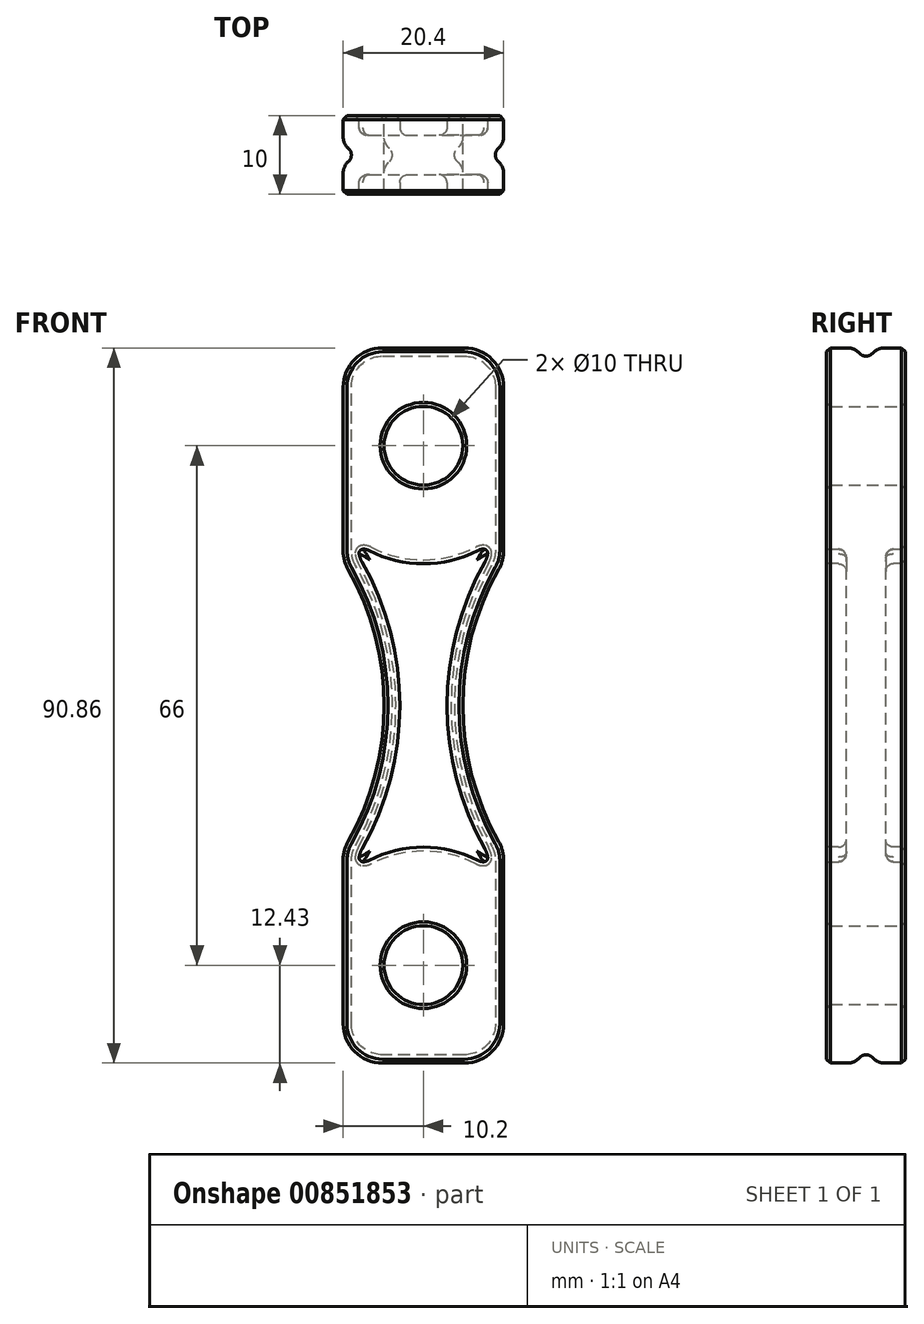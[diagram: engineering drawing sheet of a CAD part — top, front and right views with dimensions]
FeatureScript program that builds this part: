
annotation { "Feature Type Name" : "Feature", "Feature Type Description" : "" }
export const myFeature = defineFeature(function(context is Context, id is Id, definition is map)
    precondition{}
    {
        {
            var Q0;
            Q0=qCreatedBy(makeId("Front.planeOp"),FACE);
            var sketch = newSketch(context, id + "F0", { "sketchPlane" : qUnion([Q0])});
            skCircle(sketch, "E0", {"center": v(0, 33) * mm, "radius": 5 * mm});
            skCircle(sketch, "E1.MirrorC", {"center": v(0, -33) * mm, "radius": 5 * mm});
            skLineSegment(sketch, "E2.bottom", {"start": v(-5.2, 45.43) * mm, "end": v(5.2, 45.43) * mm});
            skLineSegment(sketch, "E2.top", {"start": v(-5.2, -45.43) * mm, "end": v(5.2, -45.43) * mm});
            skLineSegment(sketch, "E2.left", {"start": v(-10.2, 40.43) * mm, "end": v(-10.2, 19.73) * mm});
            skLineSegment(sketch, "E2.right", {"start": v(10.2, 40.43) * mm, "end": v(10.2, 19.73) * mm});
            skPoint(sketch, "E2.middle", {"position": v(0, 0) * mm});
            skPoint(sketch, "E3.visualSharp", {"position": v(-10.2, 45.43) * mm});
            skArc(sketch, "E3.filletArc", {"start": v(-5.2, 45.43) * mm, "mid": v(-8.74, 43.97) * mm, "end": v(-10.2, 40.43) * mm});
            skPoint(sketch, "E4.visualSharp", {"position": v(10.2, 45.43) * mm});
            skArc(sketch, "E4.filletArc", {"start": v(10.2, 40.43) * mm, "mid": v(8.74, 43.97) * mm, "end": v(5.2, 45.43) * mm});
            skPoint(sketch, "E5.visualSharp", {"position": v(-10.2, -45.43) * mm});
            skArc(sketch, "E5.filletArc", {"start": v(-10.2, -40.43) * mm, "mid": v(-8.74, -43.97) * mm, "end": v(-5.2, -45.43) * mm});
            skPoint(sketch, "E6.visualSharp", {"position": v(10.2, -45.43) * mm});
            skArc(sketch, "E6.filletArc", {"start": v(5.2, -45.43) * mm, "mid": v(8.74, -43.97) * mm, "end": v(10.2, -40.43) * mm});
            skLineSegment(sketch, "E7", {"start": v(0, 0) * mm, "end": v(-40, 0) * mm, "construction": true});
            skArc(sketch, "E8", {"start": v(-10.2, -18.36) * mm, "mid": v(-5, 0) * mm, "end": v(-10.2, 18.36) * mm});
            skLineSegment(sketch, "E9.trimOffspring", {"start": v(-10.2, -19.73) * mm, "end": v(-10.2, -40.43) * mm});
            skArc(sketch, "E10.MirrorCS", {"start": v(-10.2, 18.36) * mm, "mid": v(-5, 0) * mm, "end": v(-10.2, -18.36) * mm});
            skArc(sketch, "E11.MirrorCS", {"start": v(-9.55, -17.26) * mm, "mid": v(-5, 0) * mm, "end": v(-9.55, 17.26) * mm});
            skArc(sketch, "E12.MirrorCS", {"start": v(9.55, -17.26) * mm, "mid": v(5, 0) * mm, "end": v(9.55, 17.26) * mm});
            skLineSegment(sketch, "E13.trimOffspring", {"start": v(10.2, -19.73) * mm, "end": v(10.2, -40.43) * mm});
            skPoint(sketch, "E14.visualSharp", {"position": v(10.2, 18.36) * mm});
            skArc(sketch, "E14.filletArc", {"start": v(9.55, 17.26) * mm, "mid": v(10.04, 18.45) * mm, "end": v(10.2, 19.73) * mm});
            skPoint(sketch, "E15.visualSharp", {"position": v(-10.2, 18.36) * mm});
            skArc(sketch, "E15.filletArc", {"start": v(-10.2, 19.73) * mm, "mid": v(-10.04, 18.45) * mm, "end": v(-9.55, 17.26) * mm});
            skPoint(sketch, "E16.visualSharp", {"position": v(10.2, -18.36) * mm});
            skArc(sketch, "E16.filletArc", {"start": v(10.2, -19.73) * mm, "mid": v(10.04, -18.45) * mm, "end": v(9.55, -17.26) * mm});
            skPoint(sketch, "E17.visualSharp", {"position": v(-10.2, -18.36) * mm});
            skArc(sketch, "E17.filletArc", {"start": v(-9.55, -17.26) * mm, "mid": v(-10.04, -18.45) * mm, "end": v(-10.2, -19.73) * mm});
            skSolve(sketch);
        }
        {
            var Q0;
            Q0 = qSketchRegion(id + "F0", true);
            extrude(context, id + "F1", {"entities" : qUnion([Q0]), "depth" : 10 * mm, "offsetDistance" : 25 * mm});
        }
        {
            var Q0;
            Q0=makeQuery(id+"F1.opExtrude","CAP_EDGE",EDGE,{"disambiguationData":[OSD([sQuery(id+"F0.wireOp",EDGE,"E0")])],"isStart":false});
            var Q1;
            Q1=makeQuery(id+"F1.opExtrude","CAP_EDGE",EDGE,{"disambiguationData":[OSD([sQuery(id+"F0.wireOp",EDGE,"E0")])],"isStart":true});
            var Q2;
            Q2=makeQuery(id+"F1.opExtrude","CAP_EDGE",EDGE,{"disambiguationData":[OSD([sQuery(id+"F0.wireOp",EDGE,"E1.MirrorC")])],"isStart":false});
            var Q3;
            Q3=makeQuery(id+"F1.opExtrude","CAP_EDGE",EDGE,{"disambiguationData":[OSD([sQuery(id+"F0.wireOp",EDGE,"E1.MirrorC")])],"isStart":true});
            chamfer(context, id + "F2", {"entities" : qUnion([Q0, Q1, Q2, Q3]), "width" : 0.5 * mm, "tangentPropagation" : true});
        }
        {
            var Q0;
            Q0=qCreatedBy(makeId("Front.planeOp"),FACE);
            cPlane(context, id + "F3", {"entities" : qUnion([Q0]), "cplaneType" : CPlaneType.OFFSET, "offset" : 5 * mm, "width" : 150 * mm, "height" : 150 * mm});
        }
        {
            var Q0;
            Q0=qCreatedBy(id+"F3.planeOp",FACE);
            var sketch = newSketch(context, id + "F4", { "sketchPlane" : qUnion([Q0])});
            skArc(sketch, "E18.0.0", {"start": v(-10.2, -40.43) * mm, "mid": v(-8.74, -43.97) * mm, "end": v(-5.2, -45.43) * mm});
            skLineSegment(sketch, "E18.0.1", {"start": v(-5.2, -45.43) * mm, "end": v(5.2, -45.43) * mm});
            skArc(sketch, "E18.0.2", {"start": v(5.2, -45.43) * mm, "mid": v(8.74, -43.97) * mm, "end": v(10.2, -40.43) * mm});
            skLineSegment(sketch, "E18.0.3", {"start": v(10.2, -40.43) * mm, "end": v(10.2, -19.73) * mm});
            skArc(sketch, "E18.0.4", {"start": v(10.2, -19.73) * mm, "mid": v(10.04, -18.45) * mm, "end": v(9.55, -17.26) * mm});
            skArc(sketch, "E18.0.5", {"start": v(9.55, -17.26) * mm, "mid": v(5, 0) * mm, "end": v(9.55, 17.26) * mm});
            skArc(sketch, "E18.0.6", {"start": v(9.55, 17.26) * mm, "mid": v(10.04, 18.45) * mm, "end": v(10.2, 19.73) * mm});
            skLineSegment(sketch, "E18.0.7", {"start": v(10.2, 19.73) * mm, "end": v(10.2, 40.43) * mm});
            skArc(sketch, "E18.0.8", {"start": v(10.2, 40.43) * mm, "mid": v(8.74, 43.97) * mm, "end": v(5.2, 45.43) * mm});
            skLineSegment(sketch, "E18.0.9", {"start": v(5.2, 45.43) * mm, "end": v(-5.2, 45.43) * mm});
            skArc(sketch, "E18.0.10", {"start": v(-5.2, 45.43) * mm, "mid": v(-8.74, 43.97) * mm, "end": v(-10.2, 40.43) * mm});
            skLineSegment(sketch, "E18.0.11", {"start": v(-10.2, 40.43) * mm, "end": v(-10.2, 19.73) * mm});
            skArc(sketch, "E18.0.12", {"start": v(-10.2, 19.73) * mm, "mid": v(-10.04, 18.45) * mm, "end": v(-9.55, 17.26) * mm});
            skArc(sketch, "E18.0.13", {"start": v(-9.55, 17.26) * mm, "mid": v(-5, 0) * mm, "end": v(-9.55, -17.26) * mm});
            skArc(sketch, "E18.0.14", {"start": v(-9.55, -17.26) * mm, "mid": v(-10.04, -18.45) * mm, "end": v(-10.2, -19.73) * mm});
            skLineSegment(sketch, "E18.0.15", {"start": v(-10.2, -19.73) * mm, "end": v(-10.2, -40.43) * mm});
            skSolve(sketch);
        }
        {
            var Q0;
            Q0=qCreatedBy(makeId("Right.planeOp"),FACE);
            var sketch = newSketch(context, id + "F5", { "sketchPlane" : qUnion([Q0])});
            skCircle(sketch, "E19", {"center": v(-5, 45.5) * mm, "radius": 1.13 * mm});
            skSolve(sketch);
        }
        {
            var Q0;
            Q0=makeQuery(id+"F5.imprint","IMPRINT",FACE,{"disambiguationData":[TD([[makeQuery(id+"F5.imprint","IMPRINT",EDGE,{"derivedFrom":sQuery(id+"F5.wireOp",EDGE,"E19")}),1.0]])]});
            var Q1;
            Q1 = qConstructionFilter(qBodyType(qCreatedBy(id + "F4" ,EDGE), BodyType.WIRE), ConstructionObject.NO);
            sweep(context, id + "F6", {"operationType" : NewBodyOperationType.REMOVE, "profiles" : qUnion([Q0]), "path" : qUnion([Q1])});
        }
        {
            var Q0;
            Q0=makeQuery(id+"F6.boolean.opBoolean","INTERSECT",EDGE,{"disambiguationData":[OD(1.0)],"derivedFrom":[makeQuery(id+"F1.opExtrude","SWEPT_FACE",FACE,{"disambiguationData":[OSD([sQuery(id+"F0.wireOp",EDGE,"E4.filletArc")])]}),makeQuery(id+"F6.opSweep","SWEPT_FACE",FACE,{"disambiguationData":[OSD([sQuery(id+"F4.wireOp",EDGE,"E18.0.8"),sQuery(id+"F5.wireOp",EDGE,"E19")])]})]});
            var Q1;
            Q1=makeQuery(id+"F6.boolean.opBoolean","INTERSECT",EDGE,{"disambiguationData":[OD(0.0)],"derivedFrom":[makeQuery(id+"F1.opExtrude","SWEPT_FACE",FACE,{"disambiguationData":[OSD([sQuery(id+"F0.wireOp",EDGE,"E4.filletArc")])]}),makeQuery(id+"F6.opSweep","SWEPT_FACE",FACE,{"disambiguationData":[OSD([sQuery(id+"F4.wireOp",EDGE,"E18.0.8"),sQuery(id+"F5.wireOp",EDGE,"E19")])]})]});
            fillet(context, id + "F7", {"entities" : qUnion([Q0, Q1]), "tangentPropagation" : true, "radius" : 2 * mm, "defaultsChanged" : true, "vertexSettings" : [], "allowEdgeOverflow" : false});
        }
        {
            var Q0;
            Q0=makeQuery(id+"F1.opExtrude","CAP_FACE",FACE,{"disambiguationData":[OSD([sQuery(id+"F0.wireOp",EDGE,"E0"),sQuery(id+"F0.wireOp",EDGE,"E2.bottom"),sQuery(id+"F0.wireOp",EDGE,"E2.top"),sQuery(id+"F0.wireOp",EDGE,"E2.left"),sQuery(id+"F0.wireOp",EDGE,"E2.right"),sQuery(id+"F0.wireOp",EDGE,"E3.filletArc"),sQuery(id+"F0.wireOp",EDGE,"E4.filletArc"),sQuery(id+"F0.wireOp",EDGE,"E5.filletArc"),sQuery(id+"F0.wireOp",EDGE,"E6.filletArc"),sQuery(id+"F0.wireOp",EDGE,"E9.trimOffspring"),sQuery(id+"F0.wireOp",EDGE,"E1.MirrorC"),sQuery(id+"F0.wireOp",EDGE,"E10.MirrorCS"),sQuery(id+"F0.wireOp",EDGE,"E12.MirrorCS"),sQuery(id+"F0.wireOp",EDGE,"E13.trimOffspring"),sQuery(id+"F0.wireOp",EDGE,"E14.filletArc"),sQuery(id+"F0.wireOp",EDGE,"E15.filletArc"),sQuery(id+"F0.wireOp",EDGE,"E16.filletArc"),sQuery(id+"F0.wireOp",EDGE,"E17.filletArc")])],"isStart":false});
            var sketch = newSketch(context, id + "F8", { "sketchPlane" : qUnion([Q0])});
            skArc(sketch, "E20", {"start": v(-8.2, 20.44) * mm, "mid": v(0, 18) * mm, "end": v(8.2, 20.44) * mm});
            skArc(sketch, "E21", {"start": v(8.2, -20.44) * mm, "mid": v(0, -18) * mm, "end": v(-8.2, -20.44) * mm});
            skArc(sketch, "E22.0", {"start": v(-7.81, 18.25) * mm, "mid": v(-3, 0) * mm, "end": v(-7.81, -18.25) * mm});
            skArc(sketch, "E23.0", {"start": v(7.81, -18.25) * mm, "mid": v(3, 0) * mm, "end": v(7.81, 18.25) * mm});
            skArc(sketch, "E24.0", {"start": v(7.81, 18.25) * mm, "mid": v(8.1, 18.96) * mm, "end": v(8.2, 19.73) * mm});
            skLineSegment(sketch, "E24.1", {"start": v(8.2, 20.44) * mm, "end": v(8.2, 19.73) * mm});
            skArc(sketch, "E25.0", {"start": v(8.2, -19.73) * mm, "mid": v(8.1, -18.96) * mm, "end": v(7.81, -18.25) * mm});
            skLineSegment(sketch, "E25.1", {"start": v(8.2, -19.73) * mm, "end": v(8.2, -20.44) * mm});
            skArc(sketch, "E26.0", {"start": v(-8.2, 19.73) * mm, "mid": v(-8.1, 18.96) * mm, "end": v(-7.81, 18.25) * mm});
            skLineSegment(sketch, "E26.1", {"start": v(-8.2, 20.44) * mm, "end": v(-8.2, 19.73) * mm});
            skLineSegment(sketch, "E27.0", {"start": v(-8.2, -19.73) * mm, "end": v(-8.2, -20.44) * mm});
            skArc(sketch, "E27.1", {"start": v(-7.81, -18.25) * mm, "mid": v(-8.1, -18.96) * mm, "end": v(-8.2, -19.73) * mm});
            skSolve(sketch);
        }
        {
            var Q0;
            Q0=makeQuery(id+"F8.imprint","IMPRINT",FACE,{"disambiguationData":[TD([[makeQuery(id+"F8.imprint","IMPRINT",EDGE,{"derivedFrom":sQuery(id+"F8.wireOp",EDGE,"E20")}),-1.0]])]});
            extrude(context, id + "F9", {"entities" : qUnion([Q0]), "operationType" : NewBodyOperationType.REMOVE, "oppositeDirection" : true, "depth" : 2.5 * mm, "offsetDistance" : 25 * mm});
        }
        {
            var Q0;
            Q0=makeQuery(id+"F8.imprint","IMPRINT",FACE,{"disambiguationData":[TD([[makeQuery(id+"F8.imprint","IMPRINT",EDGE,{"derivedFrom":sQuery(id+"F8.wireOp",EDGE,"E20")}),-1.0]])]});
            extrude(context, id + "F10", {"entities" : qUnion([Q0]), "operationType" : NewBodyOperationType.REMOVE, "oppositeDirection" : true, "depth" : 34.2 * mm, "offsetDistance" : 25 * mm, "hasSecondDirection" : true, "secondDirectionOppositeDirection" : true, "secondDirectionDepth" : 7.5 * mm});
        }
        {
            var Q0;
            Q0=makeQuery(id+"F10.boolean.opBoolean","COPY",EDGE,{"derivedFrom":makeQuery(id+"F10.opExtrude","SWEPT_EDGE",EDGE,{"disambiguationData":[OSD([sQuery(id+"F8.wireOp",EDGE,"E20"),sQuery(id+"F8.wireOp",EDGE,"E24.1")])]})});
            var Q1;
            Q1=makeQuery(id+"F10.boolean.opBoolean","COPY",EDGE,{"derivedFrom":makeQuery(id+"F10.opExtrude","SWEPT_EDGE",EDGE,{"disambiguationData":[OSD([sQuery(id+"F8.wireOp",EDGE,"E20"),sQuery(id+"F8.wireOp",EDGE,"E26.1")])]})});
            var Q2;
            Q2=makeQuery(id+"F10.boolean.opBoolean","COPY",EDGE,{"derivedFrom":makeQuery(id+"F10.opExtrude","SWEPT_EDGE",EDGE,{"disambiguationData":[OSD([sQuery(id+"F8.wireOp",EDGE,"E21"),sQuery(id+"F8.wireOp",EDGE,"E25.1")])]})});
            var Q3;
            Q3=makeQuery(id+"F10.boolean.opBoolean","COPY",EDGE,{"derivedFrom":makeQuery(id+"F10.opExtrude","SWEPT_EDGE",EDGE,{"disambiguationData":[OSD([sQuery(id+"F8.wireOp",EDGE,"E21"),sQuery(id+"F8.wireOp",EDGE,"E27.0")])]})});
            var Q4;
            Q4=makeQuery(id+"F9.boolean.opBoolean","COPY",EDGE,{"derivedFrom":makeQuery(id+"F9.opExtrude","SWEPT_EDGE",EDGE,{"disambiguationData":[OSD([sQuery(id+"F8.wireOp",EDGE,"E20"),sQuery(id+"F8.wireOp",EDGE,"E26.1")])]})});
            var Q5;
            Q5=makeQuery(id+"F9.boolean.opBoolean","COPY",EDGE,{"derivedFrom":makeQuery(id+"F9.opExtrude","SWEPT_EDGE",EDGE,{"disambiguationData":[OSD([sQuery(id+"F8.wireOp",EDGE,"E20"),sQuery(id+"F8.wireOp",EDGE,"E24.1")])]})});
            var Q6;
            Q6=makeQuery(id+"F9.boolean.opBoolean","COPY",EDGE,{"derivedFrom":makeQuery(id+"F9.opExtrude","SWEPT_EDGE",EDGE,{"disambiguationData":[OSD([sQuery(id+"F8.wireOp",EDGE,"E21"),sQuery(id+"F8.wireOp",EDGE,"E25.1")])]})});
            var Q7;
            Q7=makeQuery(id+"F9.boolean.opBoolean","COPY",EDGE,{"derivedFrom":makeQuery(id+"F9.opExtrude","SWEPT_EDGE",EDGE,{"disambiguationData":[OSD([sQuery(id+"F8.wireOp",EDGE,"E21"),sQuery(id+"F8.wireOp",EDGE,"E27.0")])]})});
            fillet(context, id + "F11", {"entities" : qUnion([Q0, Q1, Q2, Q3, Q4, Q5, Q6, Q7]), "tangentPropagation" : true, "radius" : 1.5 * mm, "defaultsChanged" : false, "vertexSettings" : [], "allowEdgeOverflow" : false});
        }
        {
            var Q0;
            Q0=makeQuery(id+"F11.opFillet","BLEND_EDGE",EDGE,{"blendedFrom":[makeQuery(id+"F10.boolean.opBoolean","COPY",EDGE,{"derivedFrom":makeQuery(id+"F10.opExtrude","SWEPT_EDGE",EDGE,{"disambiguationData":[OSD([sQuery(id+"F8.wireOp",EDGE,"E20"),sQuery(id+"F8.wireOp",EDGE,"E24.1")])]})}),makeQuery(id+"F10.boolean.opBoolean","COPY",FACE,{"derivedFrom":makeQuery(id+"F10.opExtrude","SWEPT_FACE",FACE,{"disambiguationData":[OSD([sQuery(id+"F8.wireOp",EDGE,"E24.0")])]})})],"blendedInto":[makeQuery(id+"F10.boolean.opBoolean","COPY",FACE,{"derivedFrom":makeQuery(id+"F10.opExtrude","SWEPT_FACE",FACE,{"disambiguationData":[OSD([sQuery(id+"F8.wireOp",EDGE,"E24.0")])]})})]});
            var Q1;
            Q1=makeQuery(id+"F11.opFillet","BLEND_EDGE",EDGE,{"blendedFrom":[makeQuery(id+"F10.boolean.opBoolean","COPY",EDGE,{"derivedFrom":makeQuery(id+"F10.opExtrude","SWEPT_EDGE",EDGE,{"disambiguationData":[OSD([sQuery(id+"F8.wireOp",EDGE,"E20"),sQuery(id+"F8.wireOp",EDGE,"E26.1")])]})}),makeQuery(id+"F10.boolean.opBoolean","COPY",FACE,{"derivedFrom":makeQuery(id+"F10.opExtrude","SWEPT_FACE",FACE,{"disambiguationData":[OSD([sQuery(id+"F8.wireOp",EDGE,"E26.0")])]})})],"blendedInto":[makeQuery(id+"F10.boolean.opBoolean","COPY",FACE,{"derivedFrom":makeQuery(id+"F10.opExtrude","SWEPT_FACE",FACE,{"disambiguationData":[OSD([sQuery(id+"F8.wireOp",EDGE,"E26.0")])]})})]});
            var Q2;
            Q2=makeQuery(id+"F11.opFillet","BLEND_EDGE",EDGE,{"blendedFrom":[makeQuery(id+"F10.boolean.opBoolean","COPY",EDGE,{"derivedFrom":makeQuery(id+"F10.opExtrude","SWEPT_EDGE",EDGE,{"disambiguationData":[OSD([sQuery(id+"F8.wireOp",EDGE,"E21"),sQuery(id+"F8.wireOp",EDGE,"E25.1")])]})}),makeQuery(id+"F10.boolean.opBoolean","COPY",FACE,{"derivedFrom":makeQuery(id+"F10.opExtrude","SWEPT_FACE",FACE,{"disambiguationData":[OSD([sQuery(id+"F8.wireOp",EDGE,"E25.0")])]})})],"blendedInto":[makeQuery(id+"F10.boolean.opBoolean","COPY",FACE,{"derivedFrom":makeQuery(id+"F10.opExtrude","SWEPT_FACE",FACE,{"disambiguationData":[OSD([sQuery(id+"F8.wireOp",EDGE,"E25.0")])]})})]});
            var Q3;
            Q3=makeQuery(id+"F11.opFillet","BLEND_EDGE",EDGE,{"blendedFrom":[makeQuery(id+"F10.boolean.opBoolean","COPY",EDGE,{"derivedFrom":makeQuery(id+"F10.opExtrude","SWEPT_EDGE",EDGE,{"disambiguationData":[OSD([sQuery(id+"F8.wireOp",EDGE,"E21"),sQuery(id+"F8.wireOp",EDGE,"E27.0")])]})}),makeQuery(id+"F10.boolean.opBoolean","COPY",FACE,{"derivedFrom":makeQuery(id+"F10.opExtrude","SWEPT_FACE",FACE,{"disambiguationData":[OSD([sQuery(id+"F8.wireOp",EDGE,"E27.1")])]})})],"blendedInto":[makeQuery(id+"F10.boolean.opBoolean","COPY",FACE,{"derivedFrom":makeQuery(id+"F10.opExtrude","SWEPT_FACE",FACE,{"disambiguationData":[OSD([sQuery(id+"F8.wireOp",EDGE,"E27.1")])]})})]});
            var Q4;
            Q4=makeQuery(id+"F11.opFillet","BLEND_EDGE",EDGE,{"blendedFrom":[makeQuery(id+"F9.boolean.opBoolean","COPY",EDGE,{"derivedFrom":makeQuery(id+"F9.opExtrude","SWEPT_EDGE",EDGE,{"disambiguationData":[OSD([sQuery(id+"F8.wireOp",EDGE,"E21"),sQuery(id+"F8.wireOp",EDGE,"E27.0")])]})}),makeQuery(id+"F9.boolean.opBoolean","COPY",FACE,{"derivedFrom":makeQuery(id+"F9.opExtrude","SWEPT_FACE",FACE,{"disambiguationData":[OSD([sQuery(id+"F8.wireOp",EDGE,"E27.1")])]})})],"blendedInto":[makeQuery(id+"F9.boolean.opBoolean","COPY",FACE,{"derivedFrom":makeQuery(id+"F9.opExtrude","SWEPT_FACE",FACE,{"disambiguationData":[OSD([sQuery(id+"F8.wireOp",EDGE,"E27.1")])]})})]});
            var Q5;
            Q5=makeQuery(id+"F11.opFillet","BLEND_EDGE",EDGE,{"blendedFrom":[makeQuery(id+"F9.boolean.opBoolean","COPY",EDGE,{"derivedFrom":makeQuery(id+"F9.opExtrude","SWEPT_EDGE",EDGE,{"disambiguationData":[OSD([sQuery(id+"F8.wireOp",EDGE,"E21"),sQuery(id+"F8.wireOp",EDGE,"E25.1")])]})}),makeQuery(id+"F9.boolean.opBoolean","COPY",FACE,{"derivedFrom":makeQuery(id+"F9.opExtrude","SWEPT_FACE",FACE,{"disambiguationData":[OSD([sQuery(id+"F8.wireOp",EDGE,"E25.0")])]})})],"blendedInto":[makeQuery(id+"F9.boolean.opBoolean","COPY",FACE,{"derivedFrom":makeQuery(id+"F9.opExtrude","SWEPT_FACE",FACE,{"disambiguationData":[OSD([sQuery(id+"F8.wireOp",EDGE,"E25.0")])]})})]});
            var Q6;
            Q6=makeQuery(id+"F11.opFillet","BLEND_EDGE",EDGE,{"blendedFrom":[makeQuery(id+"F9.boolean.opBoolean","COPY",EDGE,{"derivedFrom":makeQuery(id+"F9.opExtrude","SWEPT_EDGE",EDGE,{"disambiguationData":[OSD([sQuery(id+"F8.wireOp",EDGE,"E20"),sQuery(id+"F8.wireOp",EDGE,"E26.1")])]})}),makeQuery(id+"F9.boolean.opBoolean","COPY",FACE,{"derivedFrom":makeQuery(id+"F9.opExtrude","SWEPT_FACE",FACE,{"disambiguationData":[OSD([sQuery(id+"F8.wireOp",EDGE,"E26.0")])]})})],"blendedInto":[makeQuery(id+"F9.boolean.opBoolean","COPY",FACE,{"derivedFrom":makeQuery(id+"F9.opExtrude","SWEPT_FACE",FACE,{"disambiguationData":[OSD([sQuery(id+"F8.wireOp",EDGE,"E26.0")])]})})]});
            var Q7;
            Q7=makeQuery(id+"F11.opFillet","BLEND_EDGE",EDGE,{"blendedFrom":[makeQuery(id+"F9.boolean.opBoolean","COPY",EDGE,{"derivedFrom":makeQuery(id+"F9.opExtrude","SWEPT_EDGE",EDGE,{"disambiguationData":[OSD([sQuery(id+"F8.wireOp",EDGE,"E20"),sQuery(id+"F8.wireOp",EDGE,"E24.1")])]})}),makeQuery(id+"F9.boolean.opBoolean","COPY",FACE,{"derivedFrom":makeQuery(id+"F9.opExtrude","SWEPT_FACE",FACE,{"disambiguationData":[OSD([sQuery(id+"F8.wireOp",EDGE,"E24.0")])]})})],"blendedInto":[makeQuery(id+"F9.boolean.opBoolean","COPY",FACE,{"derivedFrom":makeQuery(id+"F9.opExtrude","SWEPT_FACE",FACE,{"disambiguationData":[OSD([sQuery(id+"F8.wireOp",EDGE,"E24.0")])]})})]});
            fillet(context, id + "F12", {"entities" : qUnion([Q0, Q1, Q2, Q3, Q4, Q5, Q6, Q7]), "tangentPropagation" : true, "radius" : 0.5 * mm, "defaultsChanged" : false, "vertexSettings" : [], "allowEdgeOverflow" : false});
        }
        {
            var Q0;
            Q0=makeQuery(id+"F10.boolean.opBoolean","COPY",EDGE,{"derivedFrom":makeQuery(id+"F10.opExtrude","CAP_EDGE",EDGE,{"disambiguationData":[OSD([sQuery(id+"F8.wireOp",EDGE,"E23.0")])],"isStart":true})});
            var Q1;
            Q1=makeQuery(id+"F10.boolean.opBoolean","COPY",EDGE,{"derivedFrom":makeQuery(id+"F10.opExtrude","CAP_EDGE",EDGE,{"disambiguationData":[OSD([sQuery(id+"F8.wireOp",EDGE,"E22.0")])],"isStart":true})});
            var Q2;
            Q2=makeQuery(id+"F10.boolean.opBoolean","COPY",EDGE,{"derivedFrom":makeQuery(id+"F10.opExtrude","CAP_EDGE",EDGE,{"disambiguationData":[OSD([sQuery(id+"F8.wireOp",EDGE,"E24.0")])],"isStart":true})});
            var Q3;
            Q3=makeQuery(id+"F9.boolean.opBoolean","COPY",EDGE,{"derivedFrom":makeQuery(id+"F9.opExtrude","CAP_EDGE",EDGE,{"disambiguationData":[OSD([sQuery(id+"F8.wireOp",EDGE,"E20")])],"isStart":false})});
            fillet(context, id + "F13", {"entities" : qUnion([Q0, Q1, Q2, Q3]), "tangentPropagation" : true, "radius" : 1 * mm, "defaultsChanged" : false, "vertexSettings" : [], "allowEdgeOverflow" : false});
        }
        {
            var Q0;
            Q0=makeQuery(id+"F10.boolean.opBoolean","INTERSECT",EDGE,{"derivedFrom":[makeQuery(id+"F1.opExtrude","CAP_FACE",FACE,{"disambiguationData":[OSD([sQuery(id+"F0.wireOp",EDGE,"E0"),sQuery(id+"F0.wireOp",EDGE,"E2.bottom"),sQuery(id+"F0.wireOp",EDGE,"E2.top"),sQuery(id+"F0.wireOp",EDGE,"E2.left"),sQuery(id+"F0.wireOp",EDGE,"E2.right"),sQuery(id+"F0.wireOp",EDGE,"E3.filletArc"),sQuery(id+"F0.wireOp",EDGE,"E4.filletArc"),sQuery(id+"F0.wireOp",EDGE,"E5.filletArc"),sQuery(id+"F0.wireOp",EDGE,"E6.filletArc"),sQuery(id+"F0.wireOp",EDGE,"E9.trimOffspring"),sQuery(id+"F0.wireOp",EDGE,"E1.MirrorC"),sQuery(id+"F0.wireOp",EDGE,"E10.MirrorCS"),sQuery(id+"F0.wireOp",EDGE,"E12.MirrorCS"),sQuery(id+"F0.wireOp",EDGE,"E13.trimOffspring"),sQuery(id+"F0.wireOp",EDGE,"E14.filletArc"),sQuery(id+"F0.wireOp",EDGE,"E15.filletArc"),sQuery(id+"F0.wireOp",EDGE,"E16.filletArc"),sQuery(id+"F0.wireOp",EDGE,"E17.filletArc")])],"isStart":true}),makeQuery(id+"F10.opExtrude","SWEPT_FACE",FACE,{"disambiguationData":[OSD([sQuery(id+"F8.wireOp",EDGE,"E20")])]})]});
            var Q1;
            Q1=makeQuery(id+"F9.boolean.opBoolean","COPY",EDGE,{"derivedFrom":makeQuery(id+"F9.opExtrude","CAP_EDGE",EDGE,{"disambiguationData":[OSD([sQuery(id+"F8.wireOp",EDGE,"E20")])],"isStart":true})});
            chamfer(context, id + "F14", {"entities" : qUnion([Q0, Q1]), "width" : 0.5 * mm, "tangentPropagation" : true});
        }
        {
            var Q0;
            Q0=makeQuery(id+"F1.opExtrude","CAP_EDGE",EDGE,{"disambiguationData":[OSD([sQuery(id+"F0.wireOp",EDGE,"E4.filletArc")])],"isStart":true});
            var Q1;
            Q1=makeQuery(id+"F1.opExtrude","CAP_EDGE",EDGE,{"disambiguationData":[OSD([sQuery(id+"F0.wireOp",EDGE,"E4.filletArc")])],"isStart":false});
            chamfer(context, id + "F15", {"entities" : qUnion([Q0, Q1]), "width" : 0.5 * mm, "tangentPropagation" : true});
        }
    });
